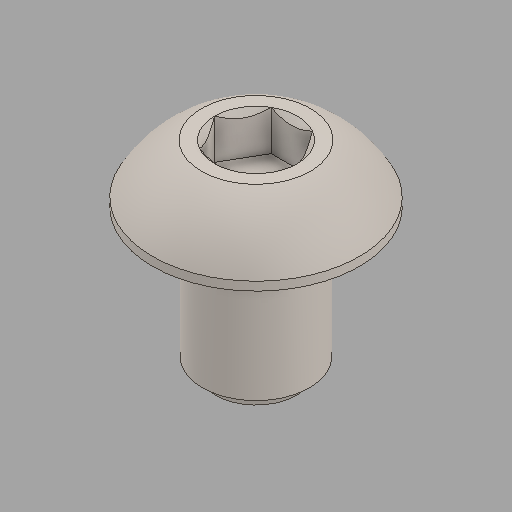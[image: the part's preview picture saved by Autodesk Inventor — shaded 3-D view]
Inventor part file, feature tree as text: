
AUTODESK INVENTOR PART (.ipt)
format: ipt  version: 2024.2 (Build 282272000, 272)  size: 136,704 bytes
history: native  units: in
note: dims shown in document units (in); Inventor stores cm internally (conversion verified against a paired STEP export)
features: fillet x1
ambient origin geometry x8: Origin, YZ Plane, XZ Plane, XY Plane, X Axis, Y Axis, Z Axis, Center Point
bodies: Solid1 (feature_tree)
feature tree (1):
  fillet  "Fillet1"  [1 undecoded]
note: 1 required parameter value undecoded (feature->parameter linkage not recoverable at this tier; creation-order binding heuristic only, values carry confidence <= 0.55)
